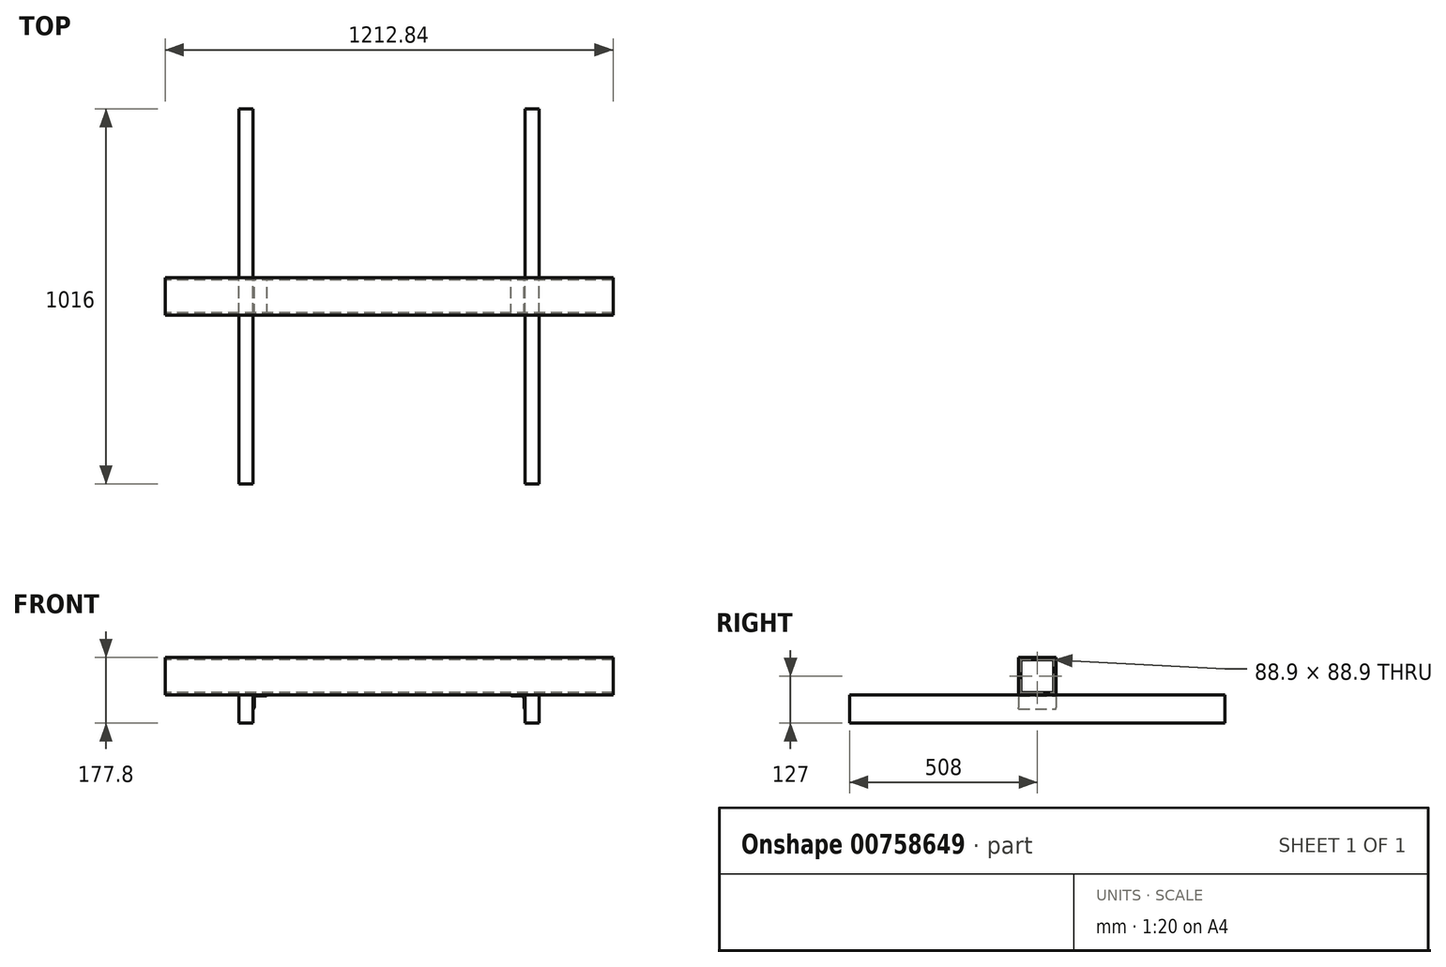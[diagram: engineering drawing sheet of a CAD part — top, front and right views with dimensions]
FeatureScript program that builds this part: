
annotation { "Feature Type Name" : "Feature", "Feature Type Description" : "" }
export const myFeature = defineFeature(function(context is Context, id is Id, definition is map)
    precondition{}
    {
        {
            var Q0;
            Q0=qCreatedBy(makeId("Front.planeOp"),FACE);
            var sketch = newSketch(context, id + "F0", { "sketchPlane" : qUnion([Q0])});
            skLineSegment(sketch, "E0.bottom", {"start": v(-406.4, 38.1) * mm, "end": v(-368.3, 38.1) * mm});
            skLineSegment(sketch, "E0.top", {"start": v(-406.4, -38.1) * mm, "end": v(-368.3, -38.1) * mm});
            skLineSegment(sketch, "E0.left", {"start": v(-406.4, 38.1) * mm, "end": v(-406.4, -38.1) * mm});
            skLineSegment(sketch, "E0.right", {"start": v(-368.3, 38.1) * mm, "end": v(-368.3, -38.1) * mm});
            skPoint(sketch, "E0.middle", {"position": v(-387.35, 0) * mm});
            skLineSegment(sketch, "E1.bottom", {"start": v(406.4, 38.1) * mm, "end": v(368.3, 38.1) * mm});
            skLineSegment(sketch, "E1.top", {"start": v(406.4, -38.1) * mm, "end": v(368.3, -38.1) * mm});
            skLineSegment(sketch, "E1.left", {"start": v(406.4, 38.1) * mm, "end": v(406.4, -38.1) * mm});
            skLineSegment(sketch, "E1.right", {"start": v(368.3, 38.1) * mm, "end": v(368.3, -38.1) * mm});
            skPoint(sketch, "E1.middle", {"position": v(387.35, 0) * mm});
            skSolve(sketch);
        }
        {
            var Q0;
            Q0 = qSketchRegion(id + "F0", true);
            extrude(context, id + "F1", {"entities" : qUnion([Q0]), "endBound" : BoundingType.SYMMETRIC, "depth" : 1016 * mm, "offsetDistance" : 25.4 * mm});
        }
        {
            var Q0;
            Q0=qCreatedBy(makeId("Right.planeOp"),FACE);
            var sketch = newSketch(context, id + "F2", { "sketchPlane" : qUnion([Q0])});
            skLineSegment(sketch, "E2.bottom", {"start": v(-50.8, 139.7) * mm, "end": v(50.8, 139.7) * mm});
            skLineSegment(sketch, "E2.top", {"start": v(-50.8, 38.1) * mm, "end": v(50.8, 38.1) * mm});
            skLineSegment(sketch, "E2.left", {"start": v(-50.8, 139.7) * mm, "end": v(-50.8, 38.1) * mm});
            skLineSegment(sketch, "E2.right", {"start": v(50.8, 139.7) * mm, "end": v(50.8, 38.1) * mm});
            skPoint(sketch, "E2.middle", {"position": v(0, 88.9) * mm});
            skLineSegment(sketch, "E3.bottom", {"start": v(-44.45, 133.35) * mm, "end": v(44.45, 133.35) * mm});
            skLineSegment(sketch, "E3.top", {"start": v(-44.45, 44.45) * mm, "end": v(44.45, 44.45) * mm});
            skLineSegment(sketch, "E3.left", {"start": v(-44.45, 133.35) * mm, "end": v(-44.45, 44.45) * mm});
            skLineSegment(sketch, "E3.right", {"start": v(44.45, 133.35) * mm, "end": v(44.45, 44.45) * mm});
            skSolve(sketch);
        }
        {
            var Q0;
            Q0 = qSketchRegion(id + "F2", true);
            extrude(context, id + "F3", {"entities" : qUnion([Q0]), "endBound" : BoundingType.SYMMETRIC, "depth" : 1212.85 * mm, "offsetDistance" : 25.4 * mm});
        }
        {
            var Q0;
            Q0=qCreatedBy(makeId("Front.planeOp"),FACE);
            var sketch = newSketch(context, id + "F4", { "sketchPlane" : qUnion([Q0])});
            skLineSegment(sketch, "E4", {"start": v(-368.3, 38.1) * mm, "end": v(-368.3, 0) * mm});
            skLineSegment(sketch, "E5", {"start": v(-368.3, 38.1) * mm, "end": v(-330.2, 38.1) * mm});
            skLineSegment(sketch, "E6", {"start": v(-330.2, 38.1) * mm, "end": v(-330.2, 38.1) * mm});
            skLineSegment(sketch, "E7", {"start": v(-333.38, 34.93) * mm, "end": v(-358.78, 34.93) * mm});
            skLineSegment(sketch, "E8", {"start": v(-365.13, 28.57) * mm, "end": v(-365.13, 3.18) * mm});
            skLineSegment(sketch, "E9", {"start": v(-368.3, 0) * mm, "end": v(-368.3, 0) * mm});
            skPoint(sketch, "E10.visualSharp", {"position": v(-365.13, 34.92) * mm});
            skArc(sketch, "E10.filletArc", {"start": v(-358.78, 34.93) * mm, "mid": v(-363.27, 33.07) * mm, "end": v(-365.13, 28.57) * mm});
            skPoint(sketch, "E11.visualSharp", {"position": v(-330.2, 34.92) * mm});
            skArc(sketch, "E11.filletArc", {"start": v(-333.38, 34.92) * mm, "mid": v(-331.13, 35.85) * mm, "end": v(-330.2, 38.1) * mm});
            skPoint(sketch, "E12.visualSharp", {"position": v(-365.13, 0) * mm});
            skArc(sketch, "E12.filletArc", {"start": v(-368.3, 0) * mm, "mid": v(-366.05, 0.93) * mm, "end": v(-365.13, 3.18) * mm});
            skArc(sketch, "E13.MirrorCS", {"start": v(368.3, 0) * mm, "mid": v(366.05, 0.93) * mm, "end": v(365.13, 3.18) * mm});
            skArc(sketch, "E14.MirrorCS", {"start": v(333.38, 34.92) * mm, "mid": v(331.13, 35.85) * mm, "end": v(330.2, 38.1) * mm});
            skArc(sketch, "E15.MirrorCS", {"start": v(358.78, 34.93) * mm, "mid": v(363.27, 33.07) * mm, "end": v(365.13, 28.57) * mm});
            skPoint(sketch, "E16.MirrorP", {"position": v(330.2, 34.92) * mm});
            skLineSegment(sketch, "E17.MirrorCS", {"start": v(368.3, 0) * mm, "end": v(368.3, 0) * mm});
            skPoint(sketch, "E18.MirrorP", {"position": v(365.13, 34.92) * mm});
            skLineSegment(sketch, "E19.MirrorCS", {"start": v(368.3, 38.1) * mm, "end": v(330.2, 38.1) * mm});
            skLineSegment(sketch, "E20.MirrorCS", {"start": v(365.13, 28.57) * mm, "end": v(365.13, 3.18) * mm});
            skLineSegment(sketch, "E21.MirrorCS", {"start": v(368.3, 38.1) * mm, "end": v(368.3, 0) * mm});
            skLineSegment(sketch, "E22.MirrorCS", {"start": v(333.38, 34.93) * mm, "end": v(358.78, 34.93) * mm});
            skPoint(sketch, "E23.MirrorP", {"position": v(365.13, 0) * mm});
            skLineSegment(sketch, "E24.MirrorCS", {"start": v(330.2, 38.1) * mm, "end": v(330.2, 38.1) * mm});
            skSolve(sketch);
        }
        {
            var Q0;
            Q0 = qSketchRegion(id + "F4", true);
            extrude(context, id + "F5", {"entities" : qUnion([Q0]), "endBound" : BoundingType.SYMMETRIC, "depth" : 101.6 * mm, "offsetDistance" : 25.4 * mm});
        }
    });
